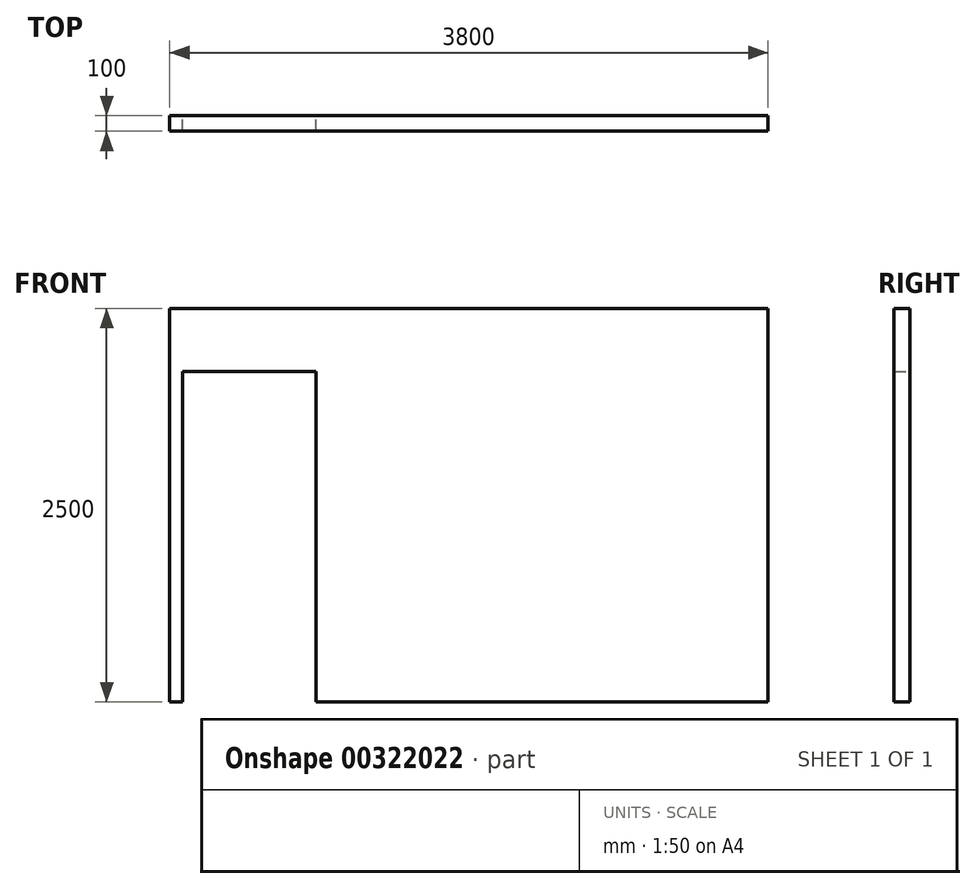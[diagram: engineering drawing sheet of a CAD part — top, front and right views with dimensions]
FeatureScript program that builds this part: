
annotation { "Feature Type Name" : "Feature", "Feature Type Description" : "" }
export const myFeature = defineFeature(function(context is Context, id is Id, definition is map)
    precondition{}
    {
        {
            var Q0;
            Q0=qCreatedBy(makeId("Front.planeOp"),FACE);
            var sketch = newSketch(context, id + "F0", { "sketchPlane" : qUnion([Q0])});
            skLineSegment(sketch, "E0.bottom", {"start": v(1900, 1250) * mm, "end": v(-1900, 1250) * mm});
            skLineSegment(sketch, "E0.top", {"start": v(1900, -1250) * mm, "end": v(-970, -1250) * mm});
            skLineSegment(sketch, "E0.left", {"start": v(1900, 1250) * mm, "end": v(1900, -1250) * mm});
            skLineSegment(sketch, "E0.right", {"start": v(-1900, 1250) * mm, "end": v(-1900, -1250) * mm});
            skPoint(sketch, "E0.middle", {"position": v(0, 0) * mm});
            skLineSegment(sketch, "E1", {"start": v(-1820, -1250) * mm, "end": v(-1820, 850) * mm});
            skLineSegment(sketch, "E2", {"start": v(-1820, 850) * mm, "end": v(-970, 850) * mm});
            skLineSegment(sketch, "E3", {"start": v(-970, 850) * mm, "end": v(-970, -1250) * mm});
            skLineSegment(sketch, "E4.trimOffspring", {"start": v(-1820, -1250) * mm, "end": v(-1900, -1250) * mm});
            skSolve(sketch);
        }
        {
            var Q0;
            Q0 = qSketchRegion(id + "F0", true);
            extrude(context, id + "F1", {"entities" : qUnion([Q0]), "depth" : 100 * mm});
        }
    });
